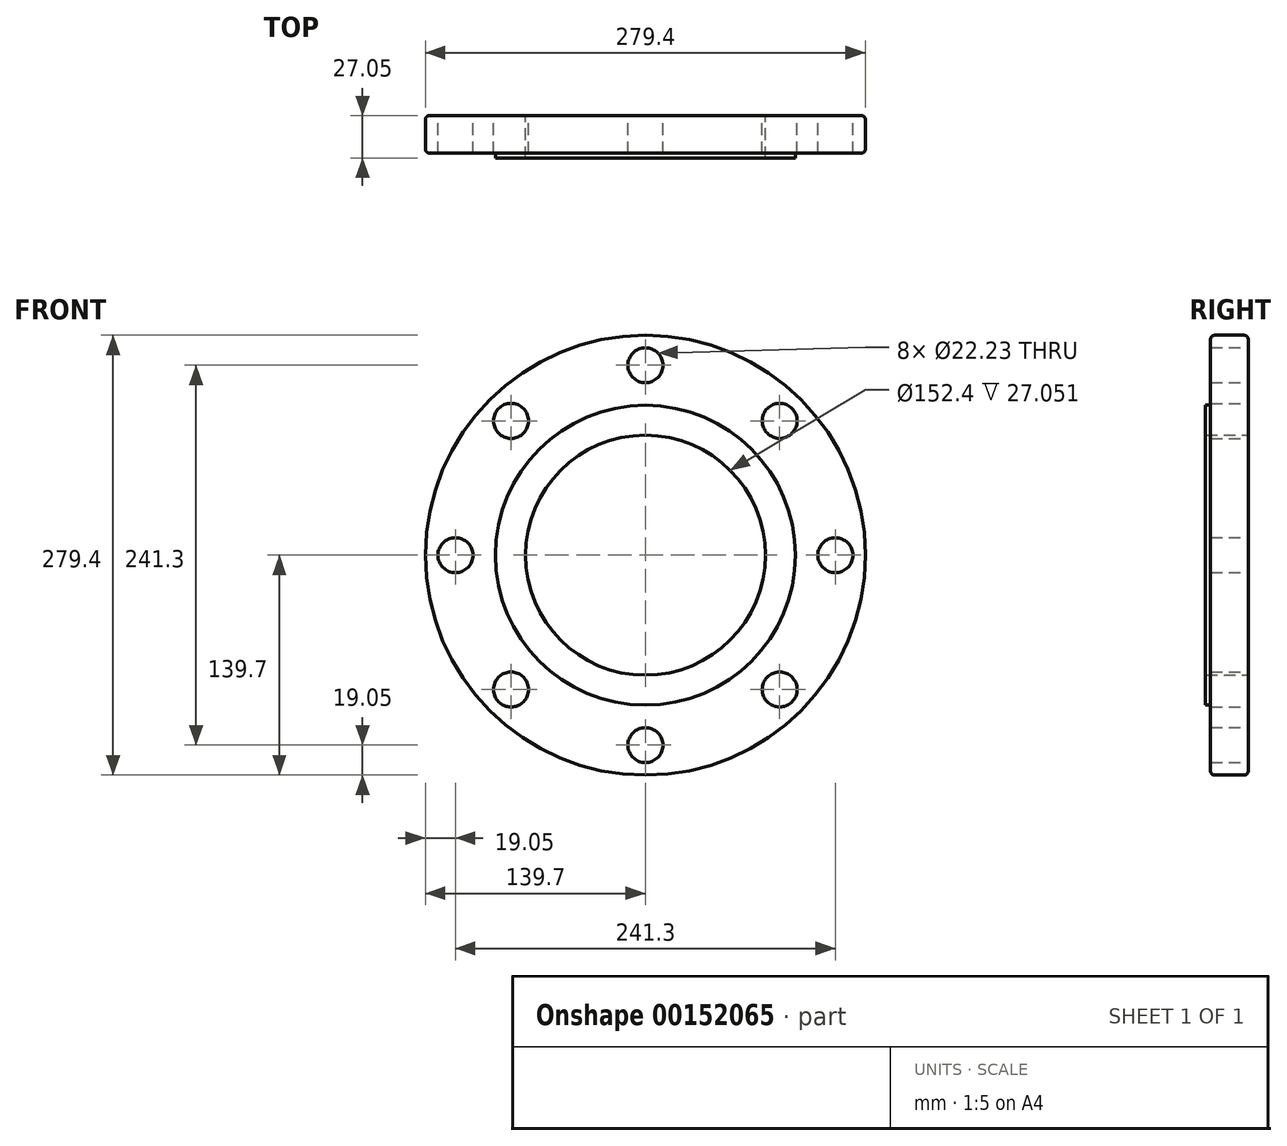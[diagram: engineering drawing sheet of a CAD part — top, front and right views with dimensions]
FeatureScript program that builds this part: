
annotation { "Feature Type Name" : "Feature", "Feature Type Description" : "" }
export const myFeature = defineFeature(function(context is Context, id is Id, definition is map)
    precondition{}
    {
        {
            var Q0;
            Q0=qCreatedBy(makeId("Front.planeOp"),FACE);
            var sketch = newSketch(context, id + "F0", { "sketchPlane" : qUnion([Q0])});
            skCircle(sketch, "E0", {"center": v(0, 0) * mm, "radius": 139.7 * mm});
            skCircle(sketch, "E1", {"center": v(0, 0) * mm, "radius": 76.2 * mm});
            skCircle(sketch, "E2", {"center": v(0, 120.65) * mm, "radius": 11.11 * mm});
            skCircle(sketch, "E3.1.0", {"center": v(-85.31, 85.31) * mm, "radius": 11.11 * mm});
            skCircle(sketch, "E3.2.0", {"center": v(-120.65, 0) * mm, "radius": 11.11 * mm});
            skCircle(sketch, "E3.3.0", {"center": v(-85.31, -85.31) * mm, "radius": 11.11 * mm});
            skCircle(sketch, "E3.4.0", {"center": v(0, -120.65) * mm, "radius": 11.11 * mm});
            skCircle(sketch, "E3.5.0", {"center": v(85.31, -85.31) * mm, "radius": 11.11 * mm});
            skCircle(sketch, "E3.6.0", {"center": v(120.65, 0) * mm, "radius": 11.11 * mm});
            skCircle(sketch, "E3.7.0", {"center": v(85.31, 85.31) * mm, "radius": 11.11 * mm});
            skSolve(sketch);
        }
        {
            var Q0;
            Q0 = qSketchRegion(id + "F0", true);
            extrude(context, id + "F1", {"entities" : qUnion([Q0]), "depth" : 23.88 * mm});
        }
        {
            var Q0;
            Q0=makeQuery(id+"F1.opExtrude","CAP_FACE",FACE,{"disambiguationData":[OSD([sQuery(id+"F0.wireOp",EDGE,"E0"),sQuery(id+"F0.wireOp",EDGE,"E1"),sQuery(id+"F0.wireOp",EDGE,"E2"),sQuery(id+"F0.wireOp",EDGE,"E3.1.0"),sQuery(id+"F0.wireOp",EDGE,"E3.2.0"),sQuery(id+"F0.wireOp",EDGE,"E3.3.0"),sQuery(id+"F0.wireOp",EDGE,"E3.4.0"),sQuery(id+"F0.wireOp",EDGE,"E3.5.0"),sQuery(id+"F0.wireOp",EDGE,"E3.6.0"),sQuery(id+"F0.wireOp",EDGE,"E3.7.0")])],"isStart":false});
            var sketch = newSketch(context, id + "F2", { "sketchPlane" : qUnion([Q0])});
            skCircle(sketch, "E4", {"center": v(0, 0) * mm, "radius": 95.25 * mm});
            skCircle(sketch, "E5", {"center": v(0, 0) * mm, "radius": 76.2 * mm});
            skSolve(sketch);
        }
        {
            var Q0;
            Q0 = qSketchRegion(id + "F2", true);
            extrude(context, id + "F3", {"entities" : qUnion([Q0]), "operationType" : NewBodyOperationType.ADD, "depth" : 3.17 * mm});
        }
        {
            var Q0;
            Q0=makeQuery(id+"F1.opExtrude","CAP_EDGE",EDGE,{"disambiguationData":[OSD([sQuery(id+"F0.wireOp",EDGE,"E0")])],"isStart":false});
            var Q1;
            Q1=makeQuery(id+"F1.opExtrude","CAP_EDGE",EDGE,{"disambiguationData":[OSD([sQuery(id+"F0.wireOp",EDGE,"E0")])],"isStart":true});
            fillet(context, id + "F4", {"entities" : qUnion([Q0, Q1]), "radius" : 2.54 * mm, "tangentPropagation" : true, "allowEdgeOverflow" : false});
        }
    });
